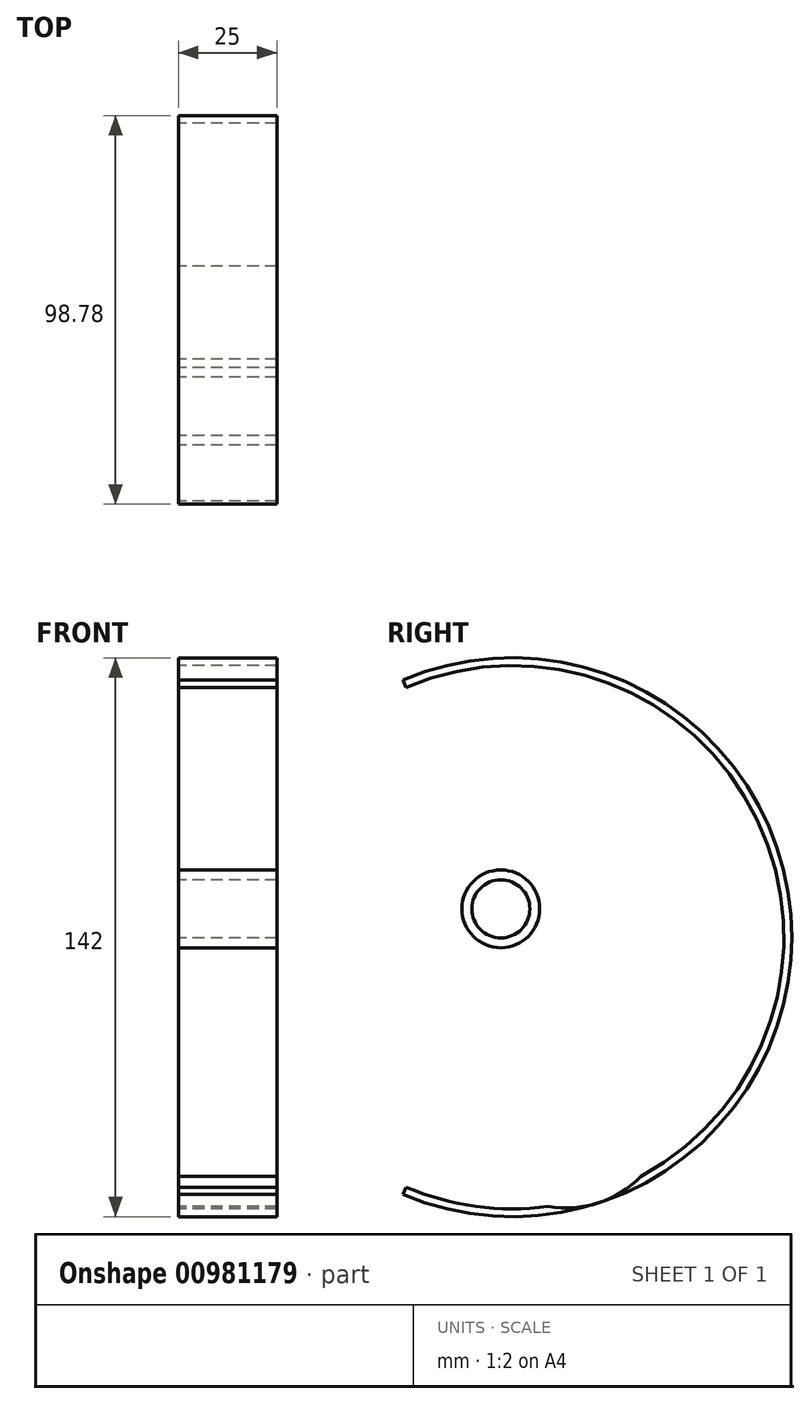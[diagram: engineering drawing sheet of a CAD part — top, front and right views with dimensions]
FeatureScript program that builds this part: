
annotation { "Feature Type Name" : "Feature", "Feature Type Description" : "" }
export const myFeature = defineFeature(function(context is Context, id is Id, definition is map)
    precondition{}
    {
        {
            var Q0;
            Q0=qCreatedBy(makeId("Right.planeOp"),FACE);
            var sketch = newSketch(context, id + "F0", { "sketchPlane" : qUnion([Q0])});
            skLineSegment(sketch, "E0", {"start": v(-76.3, 71.95) * mm, "end": v(-76.3, -78.85) * mm});
            skCircle(sketch, "E1", {"center": v(-51.42, 0) * mm, "radius": 9.88 * mm});
            skArc(sketch, "E2", {"start": v(-75.52, -70.7) * mm, "mid": v(20.48, -7.2) * mm, "end": v(-75.52, 56.29) * mm});
            skArc(sketch, "E3.0", {"start": v(-76.3, -72.55) * mm, "mid": v(22.48, -7.2) * mm, "end": v(-76.3, 58.13) * mm});
            skCircle(sketch, "E4.0", {"center": v(-51.42, 0) * mm, "radius": 7.38 * mm});
            skCircle(sketch, "E5", {"center": v(-34.8, -49.5) * mm, "radius": 26.5 * mm});
            skLineSegment(sketch, "E6", {"start": v(-76.3, 58.13) * mm, "end": v(-75.52, 56.29) * mm});
            skLineSegment(sketch, "E7", {"start": v(-76.3, -72.55) * mm, "end": v(-75.52, -70.7) * mm});
            skLineSegment(sketch, "E8", {"start": v(-38.3, 55) * mm, "end": v(-38.3, 10) * mm});
            skLineSegment(sketch, "E9", {"start": v(-66.87, 59.3) * mm, "end": v(-76.3, 55.98) * mm});
            skLineSegment(sketch, "E10", {"start": v(-76.3, 55.98) * mm, "end": v(-76.3, 45.98) * mm});
            skLineSegment(sketch, "E11", {"start": v(41.5, 30.5) * mm, "end": v(41.5, 50.61) * mm});
            skLineSegment(sketch, "E12", {"start": v(41.5, 50.61) * mm, "end": v(55.6, 55.74) * mm});
            skSolve(sketch);
        }
        {
            var Q0;
            Q0=makeQuery(id+"F0.imprint","IMPRINT",FACE,{"disambiguationData":[TD([[makeQuery(id+"F0.imprint","IMPRINT",EDGE,{"derivedFrom":sQuery(id+"F0.wireOp",EDGE,"E1")}),1.0]])]});
            var Q1;
            {var subQ0=sQuery(id+"F0.wireOp",EDGE,"E2");Q1=makeQuery(id+"F0.imprint","IMPRINT",FACE,{"disambiguationData":[TD([[makeQuery(id+"F0.imprint","IMPRINT",EDGE,{"derivedFrom":subQ0}),-1.0]])]});}
            extrude(context, id + "F1", {"entities" : qUnion([Q0, Q1]), "depth" : 25 * mm, "offsetDistance" : 25 * mm});
        }
    });
